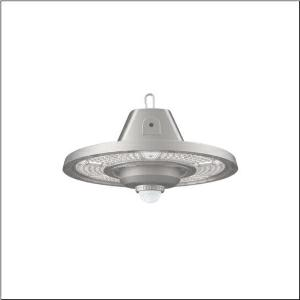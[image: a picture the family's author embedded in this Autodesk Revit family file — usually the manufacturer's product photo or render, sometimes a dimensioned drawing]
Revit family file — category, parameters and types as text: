
# Revit family: highbay_31-s_51hc427a4jmb01
name_source: partatom
category: Lighting Fixtures
units: mm (PartAtom-declared; Revit-internal decimal feet)

## family parameters
Cut with Voids When Loaded = No
Host = Face
Light Source = No
Part Type = Normal
Room Calculation Point = No
Round Connector Dimension = Use Diameter
Shared = No

## types (1)
- Highbay 31-S (1 x LED, 20000 lm, 134 W, 4000K)
    Apparent Load = 134 VA
    CIE Flux Codes = 77 99 100 100 100
    Color Rendering = 80
    Color Temperature = 4000K
    Default Elevation = 1800 mm
    Description = Highbay 31-S, LED high bay luminaire, primary light control with lens, of PC, primary optical cover: cover panel, of PC, transparent, light emission: direct distribution, primary light characteristic: rotationally symmetric, installation type: suspended mounting, surface-mounted, LED, rated luminous flux: 20.000lm, luminous efficacy: 150lm/W, light colour: 840, colour temperature: 4000K, control gear: ECG, with cable, 3x 1.0mm², free wire ends, mains connection: 220..240V, AC/DC, 0/50..60Hz, cable length: 1,5m, rated input power: 134W, housing, rotationally symmetric, of diecast aluminium, powder-coated, grey aluminium (RAL 9007), with hook on luminaire side, incl. screw, diameter: 339mm, PIR sensor, protection rating (complete): IP65, insulation class (complete): insulation class I (protective earthing), certification: CE, ENEC, UKCA, protection symbol: D, impact resistance: IK08, permissible operating ambient temperature: -30..+45°C, standard: EN 60598-2-22, EN 60598, corresponds to IFS (International Featured Standards) requirements for safety and quality in the food industry, packaging unit: 1 piece
    Height = 141 mm
    Lamp = 1 x LED
    Lamp Light Flux = 20000 lm
    Lamp Power = 134 W
    Lamp count = 1
    Length = 339 mm
    Luminous efficacy = 149 lm/W
    Manufacturer = Siteco
    ModVariant = No
    Model = 51HC427A4JMB01
    Mounting Place = Ceiling
    Mounting Type = Pendant
    Number of Poles = 1
    OnlyDefault = Yes
    Power Factor = 1
    Product Name = Highbay 31-S
    Product group = LED high bay luminaire
    ProductGroupID = 903
    Protection Class = Protection class I
    Protection Degree = IP 65
    RLX_Detail_Level = 1
    RLX_Emergency_Light_Flux = 0 lm
    RLX_Emergency_Type = 0
    RLX_Emergency_Type_DB = No
    RlxData = <blob elided: 108021 chars, md5=bd7700ec>
    Socket = socket
    Standby Power = 0 W
    System Light Flux = 20000 lm
    System Power = 134 W
    Type Comments = Product without accessories
    Type Image = l_384983.jpg
    URL = http://relux.com
    VarID = ---
    Voltage = 0 V
    Weight = 0.00 kg
    Width = 0 mm  [stored 0 ft]

note: [stored X ft] marks values corroborated as IEEE doubles in the binary element streams (Revit-internal decimal feet)

## geometry (parser evidence)
native form markers: Blend x4, Sweep x10
no freeform markers — native parametric forms only
